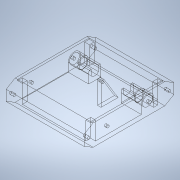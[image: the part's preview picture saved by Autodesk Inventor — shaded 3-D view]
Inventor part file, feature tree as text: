
AUTODESK INVENTOR PART (.ipt)
format: ipt  version: 2020 (Build 240168000, 168)  size: 297,472 bytes
history: native  units: in
note: dims shown in document units (in); Inventor stores cm internally (conversion verified against a paired STEP export)
features: extrude x9, sketch x9, projected_geometry x4, mirror x3, plane x1
ambient origin geometry x8: Origin, YZ Plane, XZ Plane, XY Plane, X Axis, Y Axis, Z Axis, Center Point
bodies: Solid1 (feature_tree)
feature tree (26):
  extrude  "Extrusion1"  Depth=5.9055in
  extrude  "Extrusion2"  TaperAngle=0.0deg  [1 undecoded]
  extrude  "Extrusion3"  Depth=1.2598in
  extrude  "Extrusion4"  Depth=0.315in
  extrude  "Extrusion5"  TaperAngle=0.0deg  [1 undecoded]
  extrude  "Extrusion6"  Depth=0.689in
  mirror  "Mirror1"
  extrude  "Extrusion7"  Depth=0.0787in
  mirror  "Mirror2"
  extrude  "Extrusion8"  Depth=0.5512in
  mirror  "Mirror3"
  plane  "Work Plane1"
  extrude  "Extrusion9"  Depth=0.7874in TaperAngle=0.0deg
  sketch  "Sketch1"  dims[d0=1.378in d1=5.9055in]
  sketch  "Sketch2"  dims[d2=5.1181in d3=0.0in]
  projected_geometry  "Projected Loop1"
  sketch  "Sketch3"  dims[d4=0.1575in d5=1.2598in]
  projected_geometry  "Projected Loop2"
  projected_geometry  "Projected Loop3"
  sketch  "Sketch4"  dims[d6=0.0in d8=0.315in]
  sketch  "Sketch5"  dims[d10=1.1898in d11=0.0in]
  projected_geometry  "Projected Loop4"
  sketch  "Sketch6"  dims[d12=0.6496in d13=0.689in]
  sketch  "Sketch7"  dims[d14=1.5748in d15=0.0787in]
  sketch  "Sketch9"  dims[d16=0.5512in d17=0.0in d18=0.6102in]
  sketch  "Sketch10"  dims[d19=0.4803in d20=0.7874in d21=0.0in d22=0.1654in d23=6.063in d24=0.0in d25=0.5967in d26=0.1575in d27=1.5748in d28=0.0in d29=0.0in d30=0.1575in d31=0.2756in d32=0.0in d33=0.4331in d34=0.122in d35=0.0787in d36=0.0787in d37=0.0787in d38=2.7559in d39=0.122in d40=0.061in d41=0.0787in d42=0.2362in d43=0.0in]
note: 2 required parameter values undecoded (feature->parameter linkage not recoverable at this tier; creation-order binding heuristic only, values carry confidence <= 0.55)
